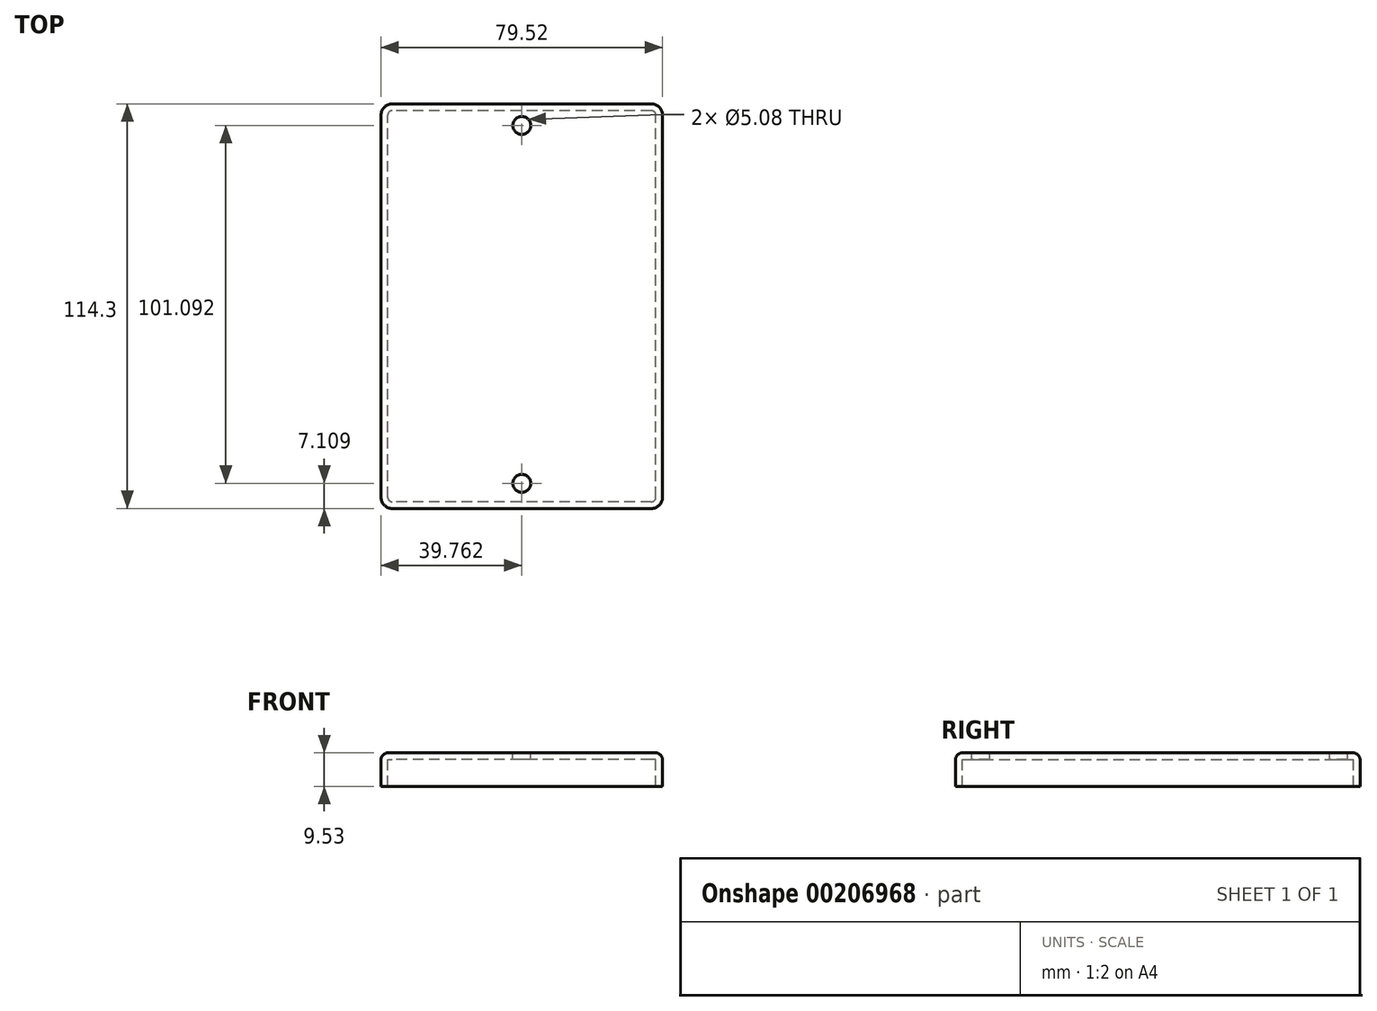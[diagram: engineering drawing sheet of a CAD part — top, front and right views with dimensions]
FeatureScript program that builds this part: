
annotation { "Feature Type Name" : "Feature", "Feature Type Description" : "" }
export const myFeature = defineFeature(function(context is Context, id is Id, definition is map)
    precondition{}
    {
        {
            var Q0;
            Q0=qCreatedBy(makeId("Top.planeOp"),FACE);
            var sketch = newSketch(context, id + "F0", { "sketchPlane" : qUnion([Q0])});
            skLineSegment(sketch, "E0", {"start": v(-66.46, 14.25) * mm, "end": v(-66.46, 122.2) * mm});
            skLineSegment(sketch, "E1", {"start": v(-145.98, 14.25) * mm, "end": v(-145.98, 122.2) * mm});
            skLineSegment(sketch, "E2", {"start": v(-69.63, 125.38) * mm, "end": v(-142.8, 125.38) * mm});
            skLineSegment(sketch, "E3", {"start": v(-69.63, 11.08) * mm, "end": v(-142.8, 11.08) * mm});
            skCircle(sketch, "E4", {"center": v(-106.22, 119.28) * mm, "radius": 2.54 * mm});
            skCircle(sketch, "E5", {"center": v(-106.22, 18.19) * mm, "radius": 2.54 * mm});
            skArc(sketch, "E6", {"start": v(-66.46, 122.2) * mm, "mid": v(-67.39, 124.45) * mm, "end": v(-69.63, 125.38) * mm});
            skArc(sketch, "E7", {"start": v(-142.8, 125.38) * mm, "mid": v(-145.05, 124.45) * mm, "end": v(-145.98, 122.2) * mm});
            skArc(sketch, "E8", {"start": v(-145.98, 14.25) * mm, "mid": v(-145.05, 12) * mm, "end": v(-142.8, 11.08) * mm});
            skArc(sketch, "E9", {"start": v(-69.63, 11.08) * mm, "mid": v(-67.39, 12) * mm, "end": v(-66.46, 14.25) * mm});
            skArc(sketch, "E10.0", {"start": v(-68.36, 122.2) * mm, "mid": v(-68.73, 123.1) * mm, "end": v(-69.63, 123.48) * mm});
            skLineSegment(sketch, "E10.1", {"start": v(-68.36, 14.25) * mm, "end": v(-68.36, 122.2) * mm});
            skLineSegment(sketch, "E10.2", {"start": v(-69.63, 123.48) * mm, "end": v(-142.8, 123.48) * mm});
            skArc(sketch, "E10.3", {"start": v(-69.63, 12.98) * mm, "mid": v(-68.73, 13.35) * mm, "end": v(-68.36, 14.25) * mm});
            skArc(sketch, "E10.4", {"start": v(-142.8, 123.48) * mm, "mid": v(-143.7, 123.1) * mm, "end": v(-144.08, 122.2) * mm});
            skLineSegment(sketch, "E10.5", {"start": v(-144.08, 14.25) * mm, "end": v(-144.08, 122.2) * mm});
            skArc(sketch, "E10.6", {"start": v(-144.08, 14.25) * mm, "mid": v(-143.7, 13.35) * mm, "end": v(-142.8, 12.98) * mm});
            skLineSegment(sketch, "E10.7", {"start": v(-69.63, 12.98) * mm, "end": v(-142.8, 12.98) * mm});
            skSolve(sketch);
        }
        {
            var Q0;
            Q0=makeQuery(id+"F0.imprint","IMPRINT",FACE,{"disambiguationData":[TD([[makeQuery(id+"F0.imprint","IMPRINT",EDGE,{"derivedFrom":sQuery(id+"F0.wireOp",EDGE,"E0")}),1.0]])]});
            extrude(context, id + "F1", {"entities" : qUnion([Q0]), "oppositeDirection" : true, "depth" : 9.52 * mm});
        }
        {
            var Q0;
            {var subQ3=sQuery(id+"F0.wireOp",EDGE,"E10.0");Q0=makeQuery(id+"F0.imprint","IMPRINT",FACE,{"disambiguationData":[TD([[makeQuery(id+"F0.imprint","IMPRINT",EDGE,{"derivedFrom":subQ3}),1.0]])]});}
            extrude(context, id + "F2", {"entities" : qUnion([Q0]), "operationType" : NewBodyOperationType.ADD, "oppositeDirection" : true, "depth" : 1.9 * mm});
        }
        {
            var Q0;
            Q0=makeQuery(id+"F1.opExtrude","CAP_EDGE",EDGE,{"disambiguationData":[OSD([sQuery(id+"F0.wireOp",EDGE,"E2")])],"isStart":true});
            fillet(context, id + "F3", {"entities" : qUnion([Q0]), "radius" : 2.03 * mm, "tangentPropagation" : true, "allowEdgeOverflow" : false});
        }
    });
